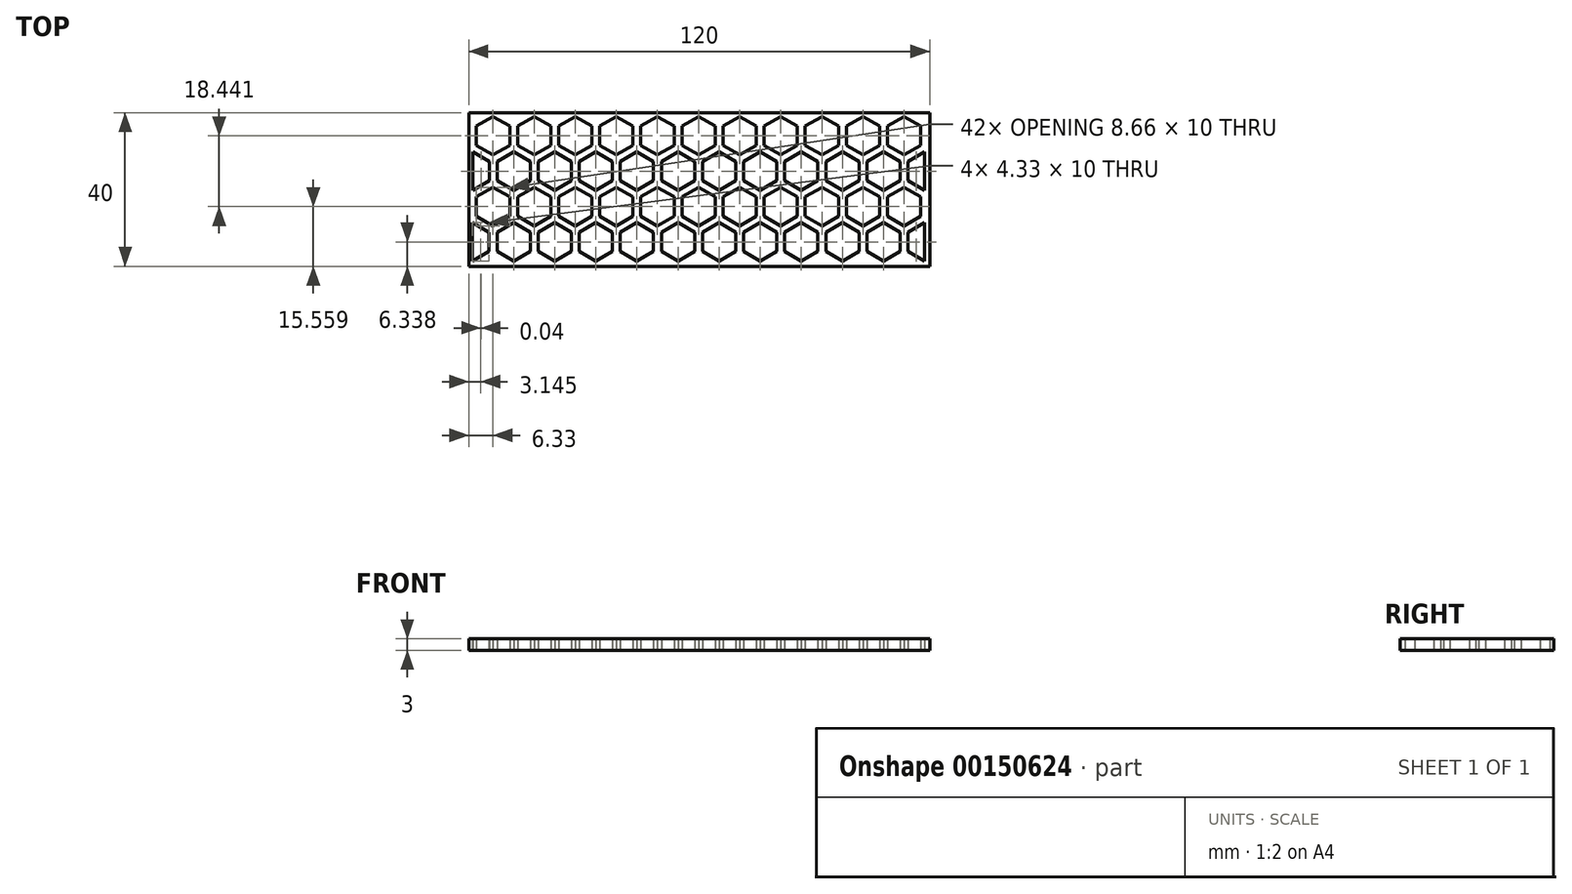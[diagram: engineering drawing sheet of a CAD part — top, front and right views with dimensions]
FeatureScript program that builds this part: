
annotation { "Feature Type Name" : "Feature", "Feature Type Description" : "" }
export const myFeature = defineFeature(function(context is Context, id is Id, definition is map)
    precondition{}
    {
        {
            var Q0;
            Q0=qCreatedBy(makeId("Top.planeOp"),FACE);
            var sketch = newSketch(context, id + "F0", { "sketchPlane" : qUnion([Q0])});
            skCircle(sketch, "E0.cCircle", {"center": v(-53.67, 14) * mm, "radius": 4.33 * mm, "construction": true});
            skLineSegment(sketch, "E0.0", {"start": v(-49.34, 11.5) * mm, "end": v(-53.67, 9) * mm});
            skLineSegment(sketch, "E0.1", {"start": v(-53.67, 9) * mm, "end": v(-58, 11.5) * mm});
            skLineSegment(sketch, "E0.2", {"start": v(-58, 11.5) * mm, "end": v(-58, 16.5) * mm});
            skLineSegment(sketch, "E0.3", {"start": v(-58, 16.5) * mm, "end": v(-53.67, 19) * mm});
            skLineSegment(sketch, "E0.4", {"start": v(-53.67, 19) * mm, "end": v(-49.34, 16.5) * mm});
            skLineSegment(sketch, "E0.5", {"start": v(-49.34, 16.5) * mm, "end": v(-49.34, 11.5) * mm});
            skPoint(sketch, "E0.0.midPoint", {"position": v(-51.5, 10.25) * mm});
            skPoint(sketch, "E1.1.0.0", {"position": v(-40.8, 10.25) * mm});
            skCircle(sketch, "E1.1.0.1", {"center": v(-42.97, 14) * mm, "radius": 4.33 * mm, "construction": true});
            skLineSegment(sketch, "E1.1.0.2", {"start": v(-38.64, 16.5) * mm, "end": v(-38.64, 11.5) * mm});
            skLineSegment(sketch, "E1.1.0.3", {"start": v(-42.97, 19) * mm, "end": v(-38.64, 16.5) * mm});
            skLineSegment(sketch, "E1.1.0.4", {"start": v(-47.3, 16.5) * mm, "end": v(-42.97, 19) * mm});
            skLineSegment(sketch, "E1.1.0.5", {"start": v(-47.3, 11.5) * mm, "end": v(-47.3, 16.5) * mm});
            skLineSegment(sketch, "E1.1.0.6", {"start": v(-38.64, 11.5) * mm, "end": v(-42.97, 9) * mm});
            skLineSegment(sketch, "E1.1.0.7", {"start": v(-42.97, 9) * mm, "end": v(-47.3, 11.5) * mm});
            skPoint(sketch, "E1.2.0.0", {"position": v(-30.1, 10.25) * mm});
            skCircle(sketch, "E1.2.0.1", {"center": v(-32.27, 14) * mm, "radius": 4.33 * mm, "construction": true});
            skLineSegment(sketch, "E1.2.0.2", {"start": v(-27.94, 16.5) * mm, "end": v(-27.94, 11.5) * mm});
            skLineSegment(sketch, "E1.2.0.3", {"start": v(-32.27, 19) * mm, "end": v(-27.94, 16.5) * mm});
            skLineSegment(sketch, "E1.2.0.4", {"start": v(-36.6, 16.5) * mm, "end": v(-32.27, 19) * mm});
            skLineSegment(sketch, "E1.2.0.5", {"start": v(-36.6, 11.5) * mm, "end": v(-36.6, 16.5) * mm});
            skLineSegment(sketch, "E1.2.0.6", {"start": v(-27.94, 11.5) * mm, "end": v(-32.27, 9) * mm});
            skLineSegment(sketch, "E1.2.0.7", {"start": v(-32.27, 9) * mm, "end": v(-36.6, 11.5) * mm});
            skPoint(sketch, "E1.3.0.0", {"position": v(-19.4, 10.25) * mm});
            skCircle(sketch, "E1.3.0.1", {"center": v(-21.57, 14) * mm, "radius": 4.33 * mm, "construction": true});
            skLineSegment(sketch, "E1.3.0.2", {"start": v(-17.24, 16.5) * mm, "end": v(-17.24, 11.5) * mm});
            skLineSegment(sketch, "E1.3.0.3", {"start": v(-21.57, 19) * mm, "end": v(-17.24, 16.5) * mm});
            skLineSegment(sketch, "E1.3.0.4", {"start": v(-25.9, 16.5) * mm, "end": v(-21.57, 19) * mm});
            skLineSegment(sketch, "E1.3.0.5", {"start": v(-25.9, 11.5) * mm, "end": v(-25.9, 16.5) * mm});
            skLineSegment(sketch, "E1.3.0.6", {"start": v(-17.24, 11.5) * mm, "end": v(-21.57, 9) * mm});
            skLineSegment(sketch, "E1.3.0.7", {"start": v(-21.57, 9) * mm, "end": v(-25.9, 11.5) * mm});
            skPoint(sketch, "E1.4.0.0", {"position": v(-8.7, 10.25) * mm});
            skCircle(sketch, "E1.4.0.1", {"center": v(-10.87, 14) * mm, "radius": 4.33 * mm, "construction": true});
            skLineSegment(sketch, "E1.4.0.2", {"start": v(-6.54, 16.5) * mm, "end": v(-6.54, 11.5) * mm});
            skLineSegment(sketch, "E1.4.0.3", {"start": v(-10.87, 19) * mm, "end": v(-6.54, 16.5) * mm});
            skLineSegment(sketch, "E1.4.0.4", {"start": v(-15.2, 16.5) * mm, "end": v(-10.87, 19) * mm});
            skLineSegment(sketch, "E1.4.0.5", {"start": v(-15.2, 11.5) * mm, "end": v(-15.2, 16.5) * mm});
            skLineSegment(sketch, "E1.4.0.6", {"start": v(-6.54, 11.5) * mm, "end": v(-10.87, 9) * mm});
            skLineSegment(sketch, "E1.4.0.7", {"start": v(-10.87, 9) * mm, "end": v(-15.2, 11.5) * mm});
            skPoint(sketch, "E1.5.0.0", {"position": v(2, 10.25) * mm});
            skCircle(sketch, "E1.5.0.1", {"center": v(-0.17, 14) * mm, "radius": 4.33 * mm, "construction": true});
            skLineSegment(sketch, "E1.5.0.2", {"start": v(4.16, 16.5) * mm, "end": v(4.16, 11.5) * mm});
            skLineSegment(sketch, "E1.5.0.3", {"start": v(-0.17, 19) * mm, "end": v(4.16, 16.5) * mm});
            skLineSegment(sketch, "E1.5.0.4", {"start": v(-4.5, 16.5) * mm, "end": v(-0.17, 19) * mm});
            skLineSegment(sketch, "E1.5.0.5", {"start": v(-4.5, 11.5) * mm, "end": v(-4.5, 16.5) * mm});
            skLineSegment(sketch, "E1.5.0.6", {"start": v(4.16, 11.5) * mm, "end": v(-0.17, 9) * mm});
            skLineSegment(sketch, "E1.5.0.7", {"start": v(-0.17, 9) * mm, "end": v(-4.5, 11.5) * mm});
            skPoint(sketch, "E1.6.0.0", {"position": v(12.7, 10.25) * mm});
            skCircle(sketch, "E1.6.0.1", {"center": v(10.53, 14) * mm, "radius": 4.33 * mm, "construction": true});
            skLineSegment(sketch, "E1.6.0.2", {"start": v(14.86, 16.5) * mm, "end": v(14.86, 11.5) * mm});
            skLineSegment(sketch, "E1.6.0.3", {"start": v(10.53, 19) * mm, "end": v(14.86, 16.5) * mm});
            skLineSegment(sketch, "E1.6.0.4", {"start": v(6.2, 16.5) * mm, "end": v(10.53, 19) * mm});
            skLineSegment(sketch, "E1.6.0.5", {"start": v(6.2, 11.5) * mm, "end": v(6.2, 16.5) * mm});
            skLineSegment(sketch, "E1.6.0.6", {"start": v(14.86, 11.5) * mm, "end": v(10.53, 9) * mm});
            skLineSegment(sketch, "E1.6.0.7", {"start": v(10.53, 9) * mm, "end": v(6.2, 11.5) * mm});
            skPoint(sketch, "E1.7.0.0", {"position": v(23.4, 10.25) * mm});
            skCircle(sketch, "E1.7.0.1", {"center": v(21.23, 14) * mm, "radius": 4.33 * mm, "construction": true});
            skLineSegment(sketch, "E1.7.0.2", {"start": v(25.56, 16.5) * mm, "end": v(25.56, 11.5) * mm});
            skLineSegment(sketch, "E1.7.0.3", {"start": v(21.23, 19) * mm, "end": v(25.56, 16.5) * mm});
            skLineSegment(sketch, "E1.7.0.4", {"start": v(16.9, 16.5) * mm, "end": v(21.23, 19) * mm});
            skLineSegment(sketch, "E1.7.0.5", {"start": v(16.9, 11.5) * mm, "end": v(16.9, 16.5) * mm});
            skLineSegment(sketch, "E1.7.0.6", {"start": v(25.56, 11.5) * mm, "end": v(21.23, 9) * mm});
            skLineSegment(sketch, "E1.7.0.7", {"start": v(21.23, 9) * mm, "end": v(16.9, 11.5) * mm});
            skPoint(sketch, "E1.8.0.0", {"position": v(34.1, 10.25) * mm});
            skCircle(sketch, "E1.8.0.1", {"center": v(31.93, 14) * mm, "radius": 4.33 * mm, "construction": true});
            skLineSegment(sketch, "E1.8.0.2", {"start": v(36.26, 16.5) * mm, "end": v(36.26, 11.5) * mm});
            skLineSegment(sketch, "E1.8.0.3", {"start": v(31.93, 19) * mm, "end": v(36.26, 16.5) * mm});
            skLineSegment(sketch, "E1.8.0.4", {"start": v(27.6, 16.5) * mm, "end": v(31.93, 19) * mm});
            skLineSegment(sketch, "E1.8.0.5", {"start": v(27.6, 11.5) * mm, "end": v(27.6, 16.5) * mm});
            skLineSegment(sketch, "E1.8.0.6", {"start": v(36.26, 11.5) * mm, "end": v(31.93, 9) * mm});
            skLineSegment(sketch, "E1.8.0.7", {"start": v(31.93, 9) * mm, "end": v(27.6, 11.5) * mm});
            skPoint(sketch, "E1.9.0.0", {"position": v(44.8, 10.25) * mm});
            skCircle(sketch, "E1.9.0.1", {"center": v(42.63, 14) * mm, "radius": 4.33 * mm, "construction": true});
            skLineSegment(sketch, "E1.9.0.2", {"start": v(46.96, 16.5) * mm, "end": v(46.96, 11.5) * mm});
            skLineSegment(sketch, "E1.9.0.3", {"start": v(42.63, 19) * mm, "end": v(46.96, 16.5) * mm});
            skLineSegment(sketch, "E1.9.0.4", {"start": v(38.3, 16.5) * mm, "end": v(42.63, 19) * mm});
            skLineSegment(sketch, "E1.9.0.5", {"start": v(38.3, 11.5) * mm, "end": v(38.3, 16.5) * mm});
            skLineSegment(sketch, "E1.9.0.6", {"start": v(46.96, 11.5) * mm, "end": v(42.63, 9) * mm});
            skLineSegment(sketch, "E1.9.0.7", {"start": v(42.63, 9) * mm, "end": v(38.3, 11.5) * mm});
            skLineSegment(sketch, "E1.direction1", {"start": v(-58, 11.5) * mm, "end": v(-47.3, 11.5) * mm, "construction": true});
            skCircle(sketch, "E2.cCircle", {"center": v(-53.67, -4.44) * mm, "radius": 4.33 * mm, "construction": true});
            skLineSegment(sketch, "E2.0", {"start": v(-49.34, -6.94) * mm, "end": v(-53.67, -9.44) * mm});
            skLineSegment(sketch, "E2.1", {"start": v(-53.67, -9.44) * mm, "end": v(-58, -6.94) * mm});
            skLineSegment(sketch, "E2.2", {"start": v(-58, -6.94) * mm, "end": v(-58, -1.94) * mm});
            skLineSegment(sketch, "E2.3", {"start": v(-58, -1.94) * mm, "end": v(-53.67, 0.56) * mm});
            skLineSegment(sketch, "E2.4", {"start": v(-53.67, 0.56) * mm, "end": v(-49.34, -1.94) * mm});
            skLineSegment(sketch, "E2.5", {"start": v(-49.34, -1.94) * mm, "end": v(-49.34, -6.94) * mm});
            skPoint(sketch, "E2.0.midPoint", {"position": v(-51.5, -8.2) * mm});
            skPoint(sketch, "E3.1.0.0", {"position": v(-40.8, -8.2) * mm});
            skCircle(sketch, "E3.1.0.1", {"center": v(-42.97, -4.44) * mm, "radius": 4.33 * mm, "construction": true});
            skLineSegment(sketch, "E3.1.0.2", {"start": v(-38.64, -1.94) * mm, "end": v(-38.64, -6.94) * mm});
            skLineSegment(sketch, "E3.1.0.3", {"start": v(-42.97, 0.56) * mm, "end": v(-38.64, -1.94) * mm});
            skLineSegment(sketch, "E3.1.0.4", {"start": v(-47.3, -1.94) * mm, "end": v(-42.97, 0.56) * mm});
            skLineSegment(sketch, "E3.1.0.5", {"start": v(-47.3, -6.94) * mm, "end": v(-47.3, -1.94) * mm});
            skLineSegment(sketch, "E3.1.0.6", {"start": v(-38.64, -6.94) * mm, "end": v(-42.97, -9.44) * mm});
            skLineSegment(sketch, "E3.1.0.7", {"start": v(-42.97, -9.44) * mm, "end": v(-47.3, -6.94) * mm});
            skPoint(sketch, "E3.2.0.0", {"position": v(-30.1, -8.2) * mm});
            skCircle(sketch, "E3.2.0.1", {"center": v(-32.27, -4.44) * mm, "radius": 4.33 * mm, "construction": true});
            skLineSegment(sketch, "E3.2.0.2", {"start": v(-27.94, -1.94) * mm, "end": v(-27.94, -6.94) * mm});
            skLineSegment(sketch, "E3.2.0.3", {"start": v(-32.27, 0.56) * mm, "end": v(-27.94, -1.94) * mm});
            skLineSegment(sketch, "E3.2.0.4", {"start": v(-36.6, -1.94) * mm, "end": v(-32.27, 0.56) * mm});
            skLineSegment(sketch, "E3.2.0.5", {"start": v(-36.6, -6.94) * mm, "end": v(-36.6, -1.94) * mm});
            skLineSegment(sketch, "E3.2.0.6", {"start": v(-27.94, -6.94) * mm, "end": v(-32.27, -9.44) * mm});
            skLineSegment(sketch, "E3.2.0.7", {"start": v(-32.27, -9.44) * mm, "end": v(-36.6, -6.94) * mm});
            skPoint(sketch, "E3.3.0.0", {"position": v(-19.4, -8.2) * mm});
            skCircle(sketch, "E3.3.0.1", {"center": v(-21.57, -4.44) * mm, "radius": 4.33 * mm, "construction": true});
            skLineSegment(sketch, "E3.3.0.2", {"start": v(-17.24, -1.94) * mm, "end": v(-17.24, -6.94) * mm});
            skLineSegment(sketch, "E3.3.0.3", {"start": v(-21.57, 0.56) * mm, "end": v(-17.24, -1.94) * mm});
            skLineSegment(sketch, "E3.3.0.4", {"start": v(-25.9, -1.94) * mm, "end": v(-21.57, 0.56) * mm});
            skLineSegment(sketch, "E3.3.0.5", {"start": v(-25.9, -6.94) * mm, "end": v(-25.9, -1.94) * mm});
            skLineSegment(sketch, "E3.3.0.6", {"start": v(-17.24, -6.94) * mm, "end": v(-21.57, -9.44) * mm});
            skLineSegment(sketch, "E3.3.0.7", {"start": v(-21.57, -9.44) * mm, "end": v(-25.9, -6.94) * mm});
            skPoint(sketch, "E3.4.0.0", {"position": v(-8.7, -8.2) * mm});
            skCircle(sketch, "E3.4.0.1", {"center": v(-10.87, -4.44) * mm, "radius": 4.33 * mm, "construction": true});
            skLineSegment(sketch, "E3.4.0.2", {"start": v(-6.54, -1.94) * mm, "end": v(-6.54, -6.94) * mm});
            skLineSegment(sketch, "E3.4.0.3", {"start": v(-10.87, 0.56) * mm, "end": v(-6.54, -1.94) * mm});
            skLineSegment(sketch, "E3.4.0.4", {"start": v(-15.2, -1.94) * mm, "end": v(-10.87, 0.56) * mm});
            skLineSegment(sketch, "E3.4.0.5", {"start": v(-15.2, -6.94) * mm, "end": v(-15.2, -1.94) * mm});
            skLineSegment(sketch, "E3.4.0.6", {"start": v(-6.54, -6.94) * mm, "end": v(-10.87, -9.44) * mm});
            skLineSegment(sketch, "E3.4.0.7", {"start": v(-10.87, -9.44) * mm, "end": v(-15.2, -6.94) * mm});
            skPoint(sketch, "E3.5.0.0", {"position": v(2, -8.2) * mm});
            skCircle(sketch, "E3.5.0.1", {"center": v(-0.17, -4.44) * mm, "radius": 4.33 * mm, "construction": true});
            skLineSegment(sketch, "E3.5.0.2", {"start": v(4.16, -1.94) * mm, "end": v(4.16, -6.94) * mm});
            skLineSegment(sketch, "E3.5.0.3", {"start": v(-0.17, 0.56) * mm, "end": v(4.16, -1.94) * mm});
            skLineSegment(sketch, "E3.5.0.4", {"start": v(-4.5, -1.94) * mm, "end": v(-0.17, 0.56) * mm});
            skLineSegment(sketch, "E3.5.0.5", {"start": v(-4.5, -6.94) * mm, "end": v(-4.5, -1.94) * mm});
            skLineSegment(sketch, "E3.5.0.6", {"start": v(4.16, -6.94) * mm, "end": v(-0.17, -9.44) * mm});
            skLineSegment(sketch, "E3.5.0.7", {"start": v(-0.17, -9.44) * mm, "end": v(-4.5, -6.94) * mm});
            skPoint(sketch, "E3.6.0.0", {"position": v(12.7, -8.2) * mm});
            skCircle(sketch, "E3.6.0.1", {"center": v(10.53, -4.44) * mm, "radius": 4.33 * mm, "construction": true});
            skLineSegment(sketch, "E3.6.0.2", {"start": v(14.86, -1.94) * mm, "end": v(14.86, -6.94) * mm});
            skLineSegment(sketch, "E3.6.0.3", {"start": v(10.53, 0.56) * mm, "end": v(14.86, -1.94) * mm});
            skLineSegment(sketch, "E3.6.0.4", {"start": v(6.2, -1.94) * mm, "end": v(10.53, 0.56) * mm});
            skLineSegment(sketch, "E3.6.0.5", {"start": v(6.2, -6.94) * mm, "end": v(6.2, -1.94) * mm});
            skLineSegment(sketch, "E3.6.0.6", {"start": v(14.86, -6.94) * mm, "end": v(10.53, -9.44) * mm});
            skLineSegment(sketch, "E3.6.0.7", {"start": v(10.53, -9.44) * mm, "end": v(6.2, -6.94) * mm});
            skPoint(sketch, "E3.7.0.0", {"position": v(23.4, -8.2) * mm});
            skCircle(sketch, "E3.7.0.1", {"center": v(21.23, -4.44) * mm, "radius": 4.33 * mm, "construction": true});
            skLineSegment(sketch, "E3.7.0.2", {"start": v(25.56, -1.94) * mm, "end": v(25.56, -6.94) * mm});
            skLineSegment(sketch, "E3.7.0.3", {"start": v(21.23, 0.56) * mm, "end": v(25.56, -1.94) * mm});
            skLineSegment(sketch, "E3.7.0.4", {"start": v(16.9, -1.94) * mm, "end": v(21.23, 0.56) * mm});
            skLineSegment(sketch, "E3.7.0.5", {"start": v(16.9, -6.94) * mm, "end": v(16.9, -1.94) * mm});
            skLineSegment(sketch, "E3.7.0.6", {"start": v(25.56, -6.94) * mm, "end": v(21.23, -9.44) * mm});
            skLineSegment(sketch, "E3.7.0.7", {"start": v(21.23, -9.44) * mm, "end": v(16.9, -6.94) * mm});
            skPoint(sketch, "E3.8.0.0", {"position": v(34.1, -8.2) * mm});
            skCircle(sketch, "E3.8.0.1", {"center": v(31.93, -4.44) * mm, "radius": 4.33 * mm, "construction": true});
            skLineSegment(sketch, "E3.8.0.2", {"start": v(36.26, -1.94) * mm, "end": v(36.26, -6.94) * mm});
            skLineSegment(sketch, "E3.8.0.3", {"start": v(31.93, 0.56) * mm, "end": v(36.26, -1.94) * mm});
            skLineSegment(sketch, "E3.8.0.4", {"start": v(27.6, -1.94) * mm, "end": v(31.93, 0.56) * mm});
            skLineSegment(sketch, "E3.8.0.5", {"start": v(27.6, -6.94) * mm, "end": v(27.6, -1.94) * mm});
            skLineSegment(sketch, "E3.8.0.6", {"start": v(36.26, -6.94) * mm, "end": v(31.93, -9.44) * mm});
            skLineSegment(sketch, "E3.8.0.7", {"start": v(31.93, -9.44) * mm, "end": v(27.6, -6.94) * mm});
            skPoint(sketch, "E3.9.0.0", {"position": v(44.8, -8.2) * mm});
            skCircle(sketch, "E3.9.0.1", {"center": v(42.63, -4.44) * mm, "radius": 4.33 * mm, "construction": true});
            skLineSegment(sketch, "E3.9.0.2", {"start": v(46.96, -1.94) * mm, "end": v(46.96, -6.94) * mm});
            skLineSegment(sketch, "E3.9.0.3", {"start": v(42.63, 0.56) * mm, "end": v(46.96, -1.94) * mm});
            skLineSegment(sketch, "E3.9.0.4", {"start": v(38.3, -1.94) * mm, "end": v(42.63, 0.56) * mm});
            skLineSegment(sketch, "E3.9.0.5", {"start": v(38.3, -6.94) * mm, "end": v(38.3, -1.94) * mm});
            skLineSegment(sketch, "E3.9.0.6", {"start": v(46.96, -6.94) * mm, "end": v(42.63, -9.44) * mm});
            skLineSegment(sketch, "E3.9.0.7", {"start": v(42.63, -9.44) * mm, "end": v(38.3, -6.94) * mm});
            skLineSegment(sketch, "E3.direction1", {"start": v(-58, -6.94) * mm, "end": v(-47.3, -6.94) * mm, "construction": true});
            skCircle(sketch, "E4.cCircle", {"center": v(-48.32, 4.78) * mm, "radius": 4.33 * mm, "construction": true});
            skLineSegment(sketch, "E4.0", {"start": v(-43.99, 2.28) * mm, "end": v(-48.32, -0.22) * mm});
            skLineSegment(sketch, "E4.1", {"start": v(-48.32, -0.22) * mm, "end": v(-52.65, 2.28) * mm});
            skLineSegment(sketch, "E4.2", {"start": v(-52.65, 2.28) * mm, "end": v(-52.65, 7.28) * mm});
            skLineSegment(sketch, "E4.3", {"start": v(-52.65, 7.28) * mm, "end": v(-48.32, 9.78) * mm});
            skLineSegment(sketch, "E4.4", {"start": v(-48.32, 9.78) * mm, "end": v(-43.99, 7.28) * mm});
            skLineSegment(sketch, "E4.5", {"start": v(-43.99, 7.28) * mm, "end": v(-43.99, 2.28) * mm});
            skPoint(sketch, "E4.0.midPoint", {"position": v(-46.15, 1.03) * mm});
            skPoint(sketch, "E5.1.0.0", {"position": v(-35.45, 1.03) * mm});
            skCircle(sketch, "E5.1.0.1", {"center": v(-37.62, 4.78) * mm, "radius": 4.33 * mm, "construction": true});
            skLineSegment(sketch, "E5.1.0.2", {"start": v(-33.29, 7.28) * mm, "end": v(-33.29, 2.28) * mm});
            skLineSegment(sketch, "E5.1.0.3", {"start": v(-37.62, 9.78) * mm, "end": v(-33.29, 7.28) * mm});
            skLineSegment(sketch, "E5.1.0.4", {"start": v(-41.95, 7.28) * mm, "end": v(-37.62, 9.78) * mm});
            skLineSegment(sketch, "E5.1.0.5", {"start": v(-41.95, 2.28) * mm, "end": v(-41.95, 7.28) * mm});
            skLineSegment(sketch, "E5.1.0.6", {"start": v(-33.29, 2.28) * mm, "end": v(-37.62, -0.22) * mm});
            skLineSegment(sketch, "E5.1.0.7", {"start": v(-37.62, -0.22) * mm, "end": v(-41.95, 2.28) * mm});
            skPoint(sketch, "E5.2.0.0", {"position": v(-24.75, 1.03) * mm});
            skCircle(sketch, "E5.2.0.1", {"center": v(-26.92, 4.78) * mm, "radius": 4.33 * mm, "construction": true});
            skLineSegment(sketch, "E5.2.0.2", {"start": v(-22.59, 7.28) * mm, "end": v(-22.59, 2.28) * mm});
            skLineSegment(sketch, "E5.2.0.3", {"start": v(-26.92, 9.78) * mm, "end": v(-22.59, 7.28) * mm});
            skLineSegment(sketch, "E5.2.0.4", {"start": v(-31.25, 7.28) * mm, "end": v(-26.92, 9.78) * mm});
            skLineSegment(sketch, "E5.2.0.5", {"start": v(-31.25, 2.28) * mm, "end": v(-31.25, 7.28) * mm});
            skLineSegment(sketch, "E5.2.0.6", {"start": v(-22.59, 2.28) * mm, "end": v(-26.92, -0.22) * mm});
            skLineSegment(sketch, "E5.2.0.7", {"start": v(-26.92, -0.22) * mm, "end": v(-31.25, 2.28) * mm});
            skPoint(sketch, "E5.3.0.0", {"position": v(-14.05, 1.03) * mm});
            skCircle(sketch, "E5.3.0.1", {"center": v(-16.22, 4.78) * mm, "radius": 4.33 * mm, "construction": true});
            skLineSegment(sketch, "E5.3.0.2", {"start": v(-11.89, 7.28) * mm, "end": v(-11.89, 2.28) * mm});
            skLineSegment(sketch, "E5.3.0.3", {"start": v(-16.22, 9.78) * mm, "end": v(-11.89, 7.28) * mm});
            skLineSegment(sketch, "E5.3.0.4", {"start": v(-20.55, 7.28) * mm, "end": v(-16.22, 9.78) * mm});
            skLineSegment(sketch, "E5.3.0.5", {"start": v(-20.55, 2.28) * mm, "end": v(-20.55, 7.28) * mm});
            skLineSegment(sketch, "E5.3.0.6", {"start": v(-11.89, 2.28) * mm, "end": v(-16.22, -0.22) * mm});
            skLineSegment(sketch, "E5.3.0.7", {"start": v(-16.22, -0.22) * mm, "end": v(-20.55, 2.28) * mm});
            skPoint(sketch, "E5.4.0.0", {"position": v(-3.35, 1.03) * mm});
            skCircle(sketch, "E5.4.0.1", {"center": v(-5.52, 4.78) * mm, "radius": 4.33 * mm, "construction": true});
            skLineSegment(sketch, "E5.4.0.2", {"start": v(-1.19, 7.28) * mm, "end": v(-1.19, 2.28) * mm});
            skLineSegment(sketch, "E5.4.0.3", {"start": v(-5.52, 9.78) * mm, "end": v(-1.19, 7.28) * mm});
            skLineSegment(sketch, "E5.4.0.4", {"start": v(-9.85, 7.28) * mm, "end": v(-5.52, 9.78) * mm});
            skLineSegment(sketch, "E5.4.0.5", {"start": v(-9.85, 2.28) * mm, "end": v(-9.85, 7.28) * mm});
            skLineSegment(sketch, "E5.4.0.6", {"start": v(-1.19, 2.28) * mm, "end": v(-5.52, -0.22) * mm});
            skLineSegment(sketch, "E5.4.0.7", {"start": v(-5.52, -0.22) * mm, "end": v(-9.85, 2.28) * mm});
            skPoint(sketch, "E5.5.0.0", {"position": v(7.35, 1.03) * mm});
            skCircle(sketch, "E5.5.0.1", {"center": v(5.18, 4.78) * mm, "radius": 4.33 * mm, "construction": true});
            skLineSegment(sketch, "E5.5.0.2", {"start": v(9.51, 7.28) * mm, "end": v(9.51, 2.28) * mm});
            skLineSegment(sketch, "E5.5.0.3", {"start": v(5.18, 9.78) * mm, "end": v(9.51, 7.28) * mm});
            skLineSegment(sketch, "E5.5.0.4", {"start": v(0.85, 7.28) * mm, "end": v(5.18, 9.78) * mm});
            skLineSegment(sketch, "E5.5.0.5", {"start": v(0.85, 2.28) * mm, "end": v(0.85, 7.28) * mm});
            skLineSegment(sketch, "E5.5.0.6", {"start": v(9.51, 2.28) * mm, "end": v(5.18, -0.22) * mm});
            skLineSegment(sketch, "E5.5.0.7", {"start": v(5.18, -0.22) * mm, "end": v(0.85, 2.28) * mm});
            skPoint(sketch, "E5.6.0.0", {"position": v(18.05, 1.03) * mm});
            skCircle(sketch, "E5.6.0.1", {"center": v(15.88, 4.78) * mm, "radius": 4.33 * mm, "construction": true});
            skLineSegment(sketch, "E5.6.0.2", {"start": v(20.21, 7.28) * mm, "end": v(20.21, 2.28) * mm});
            skLineSegment(sketch, "E5.6.0.3", {"start": v(15.88, 9.78) * mm, "end": v(20.21, 7.28) * mm});
            skLineSegment(sketch, "E5.6.0.4", {"start": v(11.55, 7.28) * mm, "end": v(15.88, 9.78) * mm});
            skLineSegment(sketch, "E5.6.0.5", {"start": v(11.55, 2.28) * mm, "end": v(11.55, 7.28) * mm});
            skLineSegment(sketch, "E5.6.0.6", {"start": v(20.21, 2.28) * mm, "end": v(15.88, -0.22) * mm});
            skLineSegment(sketch, "E5.6.0.7", {"start": v(15.88, -0.22) * mm, "end": v(11.55, 2.28) * mm});
            skPoint(sketch, "E5.7.0.0", {"position": v(28.75, 1.03) * mm});
            skCircle(sketch, "E5.7.0.1", {"center": v(26.58, 4.78) * mm, "radius": 4.33 * mm, "construction": true});
            skLineSegment(sketch, "E5.7.0.2", {"start": v(30.91, 7.28) * mm, "end": v(30.91, 2.28) * mm});
            skLineSegment(sketch, "E5.7.0.3", {"start": v(26.58, 9.78) * mm, "end": v(30.91, 7.28) * mm});
            skLineSegment(sketch, "E5.7.0.4", {"start": v(22.25, 7.28) * mm, "end": v(26.58, 9.78) * mm});
            skLineSegment(sketch, "E5.7.0.5", {"start": v(22.25, 2.28) * mm, "end": v(22.25, 7.28) * mm});
            skLineSegment(sketch, "E5.7.0.6", {"start": v(30.91, 2.28) * mm, "end": v(26.58, -0.22) * mm});
            skLineSegment(sketch, "E5.7.0.7", {"start": v(26.58, -0.22) * mm, "end": v(22.25, 2.28) * mm});
            skPoint(sketch, "E5.8.0.0", {"position": v(39.45, 1.03) * mm});
            skCircle(sketch, "E5.8.0.1", {"center": v(37.28, 4.78) * mm, "radius": 4.33 * mm, "construction": true});
            skLineSegment(sketch, "E5.8.0.2", {"start": v(41.61, 7.28) * mm, "end": v(41.61, 2.28) * mm});
            skLineSegment(sketch, "E5.8.0.3", {"start": v(37.28, 9.78) * mm, "end": v(41.61, 7.28) * mm});
            skLineSegment(sketch, "E5.8.0.4", {"start": v(32.95, 7.28) * mm, "end": v(37.28, 9.78) * mm});
            skLineSegment(sketch, "E5.8.0.5", {"start": v(32.95, 2.28) * mm, "end": v(32.95, 7.28) * mm});
            skLineSegment(sketch, "E5.8.0.6", {"start": v(41.61, 2.28) * mm, "end": v(37.28, -0.22) * mm});
            skLineSegment(sketch, "E5.8.0.7", {"start": v(37.28, -0.22) * mm, "end": v(32.95, 2.28) * mm});
            skPoint(sketch, "E5.9.0.0", {"position": v(50.15, 1.03) * mm});
            skCircle(sketch, "E5.9.0.1", {"center": v(47.98, 4.78) * mm, "radius": 4.33 * mm, "construction": true});
            skLineSegment(sketch, "E5.9.0.2", {"start": v(52.31, 7.28) * mm, "end": v(52.31, 2.28) * mm});
            skLineSegment(sketch, "E5.9.0.3", {"start": v(47.98, 9.78) * mm, "end": v(52.31, 7.28) * mm});
            skLineSegment(sketch, "E5.9.0.4", {"start": v(43.65, 7.28) * mm, "end": v(47.98, 9.78) * mm});
            skLineSegment(sketch, "E5.9.0.5", {"start": v(43.65, 2.28) * mm, "end": v(43.65, 7.28) * mm});
            skLineSegment(sketch, "E5.9.0.6", {"start": v(52.31, 2.28) * mm, "end": v(47.98, -0.22) * mm});
            skLineSegment(sketch, "E5.9.0.7", {"start": v(47.98, -0.22) * mm, "end": v(43.65, 2.28) * mm});
            skLineSegment(sketch, "E5.direction1", {"start": v(-52.65, 2.28) * mm, "end": v(-41.95, 2.28) * mm, "construction": true});
            skLineSegment(sketch, "E6.cCircle", {"start": v(-62.56, -16.16) * mm, "end": v(-62.56, -16.16) * mm});
            skLineSegment(sketch, "E6.0", {"start": v(-54.69, -16.16) * mm, "end": v(-59.02, -18.66) * mm});
            skLineSegment(sketch, "E6.4", {"start": v(-59.02, -8.66) * mm, "end": v(-54.69, -11.16) * mm});
            skLineSegment(sketch, "E6.5", {"start": v(-54.69, -11.16) * mm, "end": v(-54.69, -16.16) * mm});
            skPoint(sketch, "E6.0.midPoint", {"position": v(-56.85, -17.41) * mm});
            skPoint(sketch, "E7.1.0.0", {"position": v(-46.15, -17.41) * mm});
            skCircle(sketch, "E7.1.0.1", {"center": v(-48.32, -13.66) * mm, "radius": 4.33 * mm, "construction": true});
            skLineSegment(sketch, "E7.1.0.2", {"start": v(-43.99, -11.16) * mm, "end": v(-43.99, -16.16) * mm});
            skLineSegment(sketch, "E7.1.0.3", {"start": v(-48.32, -8.66) * mm, "end": v(-43.99, -11.16) * mm});
            skLineSegment(sketch, "E7.1.0.4", {"start": v(-52.65, -11.16) * mm, "end": v(-48.32, -8.66) * mm});
            skLineSegment(sketch, "E7.1.0.5", {"start": v(-52.65, -16.16) * mm, "end": v(-52.65, -11.16) * mm});
            skLineSegment(sketch, "E7.1.0.6", {"start": v(-43.99, -16.16) * mm, "end": v(-48.32, -18.66) * mm});
            skLineSegment(sketch, "E7.1.0.7", {"start": v(-48.32, -18.66) * mm, "end": v(-52.65, -16.16) * mm});
            skPoint(sketch, "E7.2.0.0", {"position": v(-35.45, -17.41) * mm});
            skCircle(sketch, "E7.2.0.1", {"center": v(-37.62, -13.66) * mm, "radius": 4.33 * mm, "construction": true});
            skLineSegment(sketch, "E7.2.0.2", {"start": v(-33.29, -11.16) * mm, "end": v(-33.29, -16.16) * mm});
            skLineSegment(sketch, "E7.2.0.3", {"start": v(-37.62, -8.66) * mm, "end": v(-33.29, -11.16) * mm});
            skLineSegment(sketch, "E7.2.0.4", {"start": v(-41.95, -11.16) * mm, "end": v(-37.62, -8.66) * mm});
            skLineSegment(sketch, "E7.2.0.5", {"start": v(-41.95, -16.16) * mm, "end": v(-41.95, -11.16) * mm});
            skLineSegment(sketch, "E7.2.0.6", {"start": v(-33.29, -16.16) * mm, "end": v(-37.62, -18.66) * mm});
            skLineSegment(sketch, "E7.2.0.7", {"start": v(-37.62, -18.66) * mm, "end": v(-41.95, -16.16) * mm});
            skPoint(sketch, "E7.3.0.0", {"position": v(-24.75, -17.41) * mm});
            skCircle(sketch, "E7.3.0.1", {"center": v(-26.92, -13.66) * mm, "radius": 4.33 * mm, "construction": true});
            skLineSegment(sketch, "E7.3.0.2", {"start": v(-22.59, -11.16) * mm, "end": v(-22.59, -16.16) * mm});
            skLineSegment(sketch, "E7.3.0.3", {"start": v(-26.92, -8.66) * mm, "end": v(-22.59, -11.16) * mm});
            skLineSegment(sketch, "E7.3.0.4", {"start": v(-31.25, -11.16) * mm, "end": v(-26.92, -8.66) * mm});
            skLineSegment(sketch, "E7.3.0.5", {"start": v(-31.25, -16.16) * mm, "end": v(-31.25, -11.16) * mm});
            skLineSegment(sketch, "E7.3.0.6", {"start": v(-22.59, -16.16) * mm, "end": v(-26.92, -18.66) * mm});
            skLineSegment(sketch, "E7.3.0.7", {"start": v(-26.92, -18.66) * mm, "end": v(-31.25, -16.16) * mm});
            skPoint(sketch, "E7.4.0.0", {"position": v(-14.05, -17.41) * mm});
            skCircle(sketch, "E7.4.0.1", {"center": v(-16.22, -13.66) * mm, "radius": 4.33 * mm, "construction": true});
            skLineSegment(sketch, "E7.4.0.2", {"start": v(-11.89, -11.16) * mm, "end": v(-11.89, -16.16) * mm});
            skLineSegment(sketch, "E7.4.0.3", {"start": v(-16.22, -8.66) * mm, "end": v(-11.89, -11.16) * mm});
            skLineSegment(sketch, "E7.4.0.4", {"start": v(-20.55, -11.16) * mm, "end": v(-16.22, -8.66) * mm});
            skLineSegment(sketch, "E7.4.0.5", {"start": v(-20.55, -16.16) * mm, "end": v(-20.55, -11.16) * mm});
            skLineSegment(sketch, "E7.4.0.6", {"start": v(-11.89, -16.16) * mm, "end": v(-16.22, -18.66) * mm});
            skLineSegment(sketch, "E7.4.0.7", {"start": v(-16.22, -18.66) * mm, "end": v(-20.55, -16.16) * mm});
            skPoint(sketch, "E7.5.0.0", {"position": v(-3.35, -17.41) * mm});
            skCircle(sketch, "E7.5.0.1", {"center": v(-5.52, -13.66) * mm, "radius": 4.33 * mm, "construction": true});
            skLineSegment(sketch, "E7.5.0.2", {"start": v(-1.19, -11.16) * mm, "end": v(-1.19, -16.16) * mm});
            skLineSegment(sketch, "E7.5.0.3", {"start": v(-5.52, -8.66) * mm, "end": v(-1.19, -11.16) * mm});
            skLineSegment(sketch, "E7.5.0.4", {"start": v(-9.85, -11.16) * mm, "end": v(-5.52, -8.66) * mm});
            skLineSegment(sketch, "E7.5.0.5", {"start": v(-9.85, -16.16) * mm, "end": v(-9.85, -11.16) * mm});
            skLineSegment(sketch, "E7.5.0.6", {"start": v(-1.19, -16.16) * mm, "end": v(-5.52, -18.66) * mm});
            skLineSegment(sketch, "E7.5.0.7", {"start": v(-5.52, -18.66) * mm, "end": v(-9.85, -16.16) * mm});
            skPoint(sketch, "E7.6.0.0", {"position": v(7.35, -17.41) * mm});
            skCircle(sketch, "E7.6.0.1", {"center": v(5.18, -13.66) * mm, "radius": 4.33 * mm, "construction": true});
            skLineSegment(sketch, "E7.6.0.2", {"start": v(9.51, -11.16) * mm, "end": v(9.51, -16.16) * mm});
            skLineSegment(sketch, "E7.6.0.3", {"start": v(5.18, -8.66) * mm, "end": v(9.51, -11.16) * mm});
            skLineSegment(sketch, "E7.6.0.4", {"start": v(0.85, -11.16) * mm, "end": v(5.18, -8.66) * mm});
            skLineSegment(sketch, "E7.6.0.5", {"start": v(0.85, -16.16) * mm, "end": v(0.85, -11.16) * mm});
            skLineSegment(sketch, "E7.6.0.6", {"start": v(9.51, -16.16) * mm, "end": v(5.18, -18.66) * mm});
            skLineSegment(sketch, "E7.6.0.7", {"start": v(5.18, -18.66) * mm, "end": v(0.85, -16.16) * mm});
            skPoint(sketch, "E7.7.0.0", {"position": v(18.05, -17.41) * mm});
            skCircle(sketch, "E7.7.0.1", {"center": v(15.88, -13.66) * mm, "radius": 4.33 * mm, "construction": true});
            skLineSegment(sketch, "E7.7.0.2", {"start": v(20.21, -11.16) * mm, "end": v(20.21, -16.16) * mm});
            skLineSegment(sketch, "E7.7.0.3", {"start": v(15.88, -8.66) * mm, "end": v(20.21, -11.16) * mm});
            skLineSegment(sketch, "E7.7.0.4", {"start": v(11.55, -11.16) * mm, "end": v(15.88, -8.66) * mm});
            skLineSegment(sketch, "E7.7.0.5", {"start": v(11.55, -16.16) * mm, "end": v(11.55, -11.16) * mm});
            skLineSegment(sketch, "E7.7.0.6", {"start": v(20.21, -16.16) * mm, "end": v(15.88, -18.66) * mm});
            skLineSegment(sketch, "E7.7.0.7", {"start": v(15.88, -18.66) * mm, "end": v(11.55, -16.16) * mm});
            skPoint(sketch, "E7.8.0.0", {"position": v(28.75, -17.41) * mm});
            skCircle(sketch, "E7.8.0.1", {"center": v(26.58, -13.66) * mm, "radius": 4.33 * mm, "construction": true});
            skLineSegment(sketch, "E7.8.0.2", {"start": v(30.91, -11.16) * mm, "end": v(30.91, -16.16) * mm});
            skLineSegment(sketch, "E7.8.0.3", {"start": v(26.58, -8.66) * mm, "end": v(30.91, -11.16) * mm});
            skLineSegment(sketch, "E7.8.0.4", {"start": v(22.25, -11.16) * mm, "end": v(26.58, -8.66) * mm});
            skLineSegment(sketch, "E7.8.0.5", {"start": v(22.25, -16.16) * mm, "end": v(22.25, -11.16) * mm});
            skLineSegment(sketch, "E7.8.0.6", {"start": v(30.91, -16.16) * mm, "end": v(26.58, -18.66) * mm});
            skLineSegment(sketch, "E7.8.0.7", {"start": v(26.58, -18.66) * mm, "end": v(22.25, -16.16) * mm});
            skPoint(sketch, "E7.9.0.0", {"position": v(39.45, -17.41) * mm});
            skCircle(sketch, "E7.9.0.1", {"center": v(37.28, -13.66) * mm, "radius": 4.33 * mm, "construction": true});
            skLineSegment(sketch, "E7.9.0.2", {"start": v(41.61, -11.16) * mm, "end": v(41.61, -16.16) * mm});
            skLineSegment(sketch, "E7.9.0.3", {"start": v(37.28, -8.66) * mm, "end": v(41.61, -11.16) * mm});
            skLineSegment(sketch, "E7.9.0.4", {"start": v(32.95, -11.16) * mm, "end": v(37.28, -8.66) * mm});
            skLineSegment(sketch, "E7.9.0.5", {"start": v(32.95, -16.16) * mm, "end": v(32.95, -11.16) * mm});
            skLineSegment(sketch, "E7.9.0.6", {"start": v(41.61, -16.16) * mm, "end": v(37.28, -18.66) * mm});
            skLineSegment(sketch, "E7.9.0.7", {"start": v(37.28, -18.66) * mm, "end": v(32.95, -16.16) * mm});
            skLineSegment(sketch, "E7.direction1", {"start": v(-63.35, -16.16) * mm, "end": v(-62.56, -16.16) * mm, "construction": true});
            skLineSegment(sketch, "E8.bottom", {"start": v(60, -20) * mm, "end": v(-60, -20) * mm});
            skLineSegment(sketch, "E8.top", {"start": v(60, 20) * mm, "end": v(-60, 20) * mm});
            skLineSegment(sketch, "E8.left", {"start": v(60, -20) * mm, "end": v(60, 20) * mm});
            skLineSegment(sketch, "E8.right", {"start": v(-60, -20) * mm, "end": v(-60, 20) * mm});
            skPoint(sketch, "E8.middle", {"position": v(0, 0) * mm});
            skPoint(sketch, "E9.0.10.0", {"position": v(55.5, 10.25) * mm});
            skCircle(sketch, "E9.1.10.0", {"center": v(53.33, 14) * mm, "radius": 4.33 * mm, "construction": true});
            skLineSegment(sketch, "E9.3.10.0", {"start": v(57.66, 16.5) * mm, "end": v(57.66, 11.5) * mm});
            skLineSegment(sketch, "E9.6.10.0", {"start": v(53.33, 19) * mm, "end": v(57.66, 16.5) * mm});
            skLineSegment(sketch, "E9.9.10.0", {"start": v(49, 16.5) * mm, "end": v(53.33, 19) * mm});
            skLineSegment(sketch, "E9.12.10.0", {"start": v(49, 11.5) * mm, "end": v(49, 16.5) * mm});
            skLineSegment(sketch, "E9.15.10.0", {"start": v(57.66, 11.5) * mm, "end": v(53.33, 9) * mm});
            skLineSegment(sketch, "E9.18.10.0", {"start": v(53.33, 9) * mm, "end": v(49, 11.5) * mm});
            skArc(sketch, "E10.1.10.0", {"start": v(58.68, 9.1) * mm, "mid": v(54.35, 4.78) * mm, "end": v(58.68, 0.45) * mm, "construction": true});
            skLineSegment(sketch, "E10.9.10.0", {"start": v(54.35, 7.28) * mm, "end": v(58.68, 9.78) * mm});
            skLineSegment(sketch, "E10.12.10.0", {"start": v(54.35, 2.28) * mm, "end": v(54.35, 7.28) * mm});
            skLineSegment(sketch, "E10.18.10.0", {"start": v(58.68, -0.22) * mm, "end": v(54.35, 2.28) * mm});
            skPoint(sketch, "E11.0.10.0", {"position": v(55.5, -8.2) * mm});
            skCircle(sketch, "E11.1.10.0", {"center": v(53.33, -4.44) * mm, "radius": 4.33 * mm, "construction": true});
            skLineSegment(sketch, "E11.3.10.0", {"start": v(57.66, -1.94) * mm, "end": v(57.66, -6.94) * mm});
            skLineSegment(sketch, "E11.6.10.0", {"start": v(53.33, 0.56) * mm, "end": v(57.66, -1.94) * mm});
            skLineSegment(sketch, "E11.9.10.0", {"start": v(49, -1.94) * mm, "end": v(53.33, 0.56) * mm});
            skLineSegment(sketch, "E11.12.10.0", {"start": v(49, -6.94) * mm, "end": v(49, -1.94) * mm});
            skLineSegment(sketch, "E11.15.10.0", {"start": v(57.66, -6.94) * mm, "end": v(53.33, -9.44) * mm});
            skLineSegment(sketch, "E11.18.10.0", {"start": v(53.33, -9.44) * mm, "end": v(49, -6.94) * mm});
            skPoint(sketch, "E12.0.10.0", {"position": v(50.15, -17.41) * mm});
            skCircle(sketch, "E12.1.10.0", {"center": v(47.98, -13.66) * mm, "radius": 4.33 * mm, "construction": true});
            skLineSegment(sketch, "E12.3.10.0", {"start": v(52.31, -11.16) * mm, "end": v(52.31, -16.16) * mm});
            skLineSegment(sketch, "E12.6.10.0", {"start": v(47.98, -8.66) * mm, "end": v(52.31, -11.16) * mm});
            skLineSegment(sketch, "E12.9.10.0", {"start": v(43.65, -11.16) * mm, "end": v(47.98, -8.66) * mm});
            skLineSegment(sketch, "E12.12.10.0", {"start": v(43.65, -16.16) * mm, "end": v(43.65, -11.16) * mm});
            skLineSegment(sketch, "E12.15.10.0", {"start": v(52.31, -16.16) * mm, "end": v(47.98, -18.66) * mm});
            skLineSegment(sketch, "E12.18.10.0", {"start": v(47.98, -18.66) * mm, "end": v(43.65, -16.16) * mm});
            skArc(sketch, "E12.1.11.0", {"start": v(58.68, -9.33) * mm, "mid": v(54.35, -13.66) * mm, "end": v(58.68, -18) * mm, "construction": true});
            skLineSegment(sketch, "E12.9.11.0", {"start": v(54.35, -11.16) * mm, "end": v(58.68, -8.66) * mm});
            skLineSegment(sketch, "E12.12.11.0", {"start": v(54.35, -16.16) * mm, "end": v(54.35, -11.16) * mm});
            skLineSegment(sketch, "E12.18.11.0", {"start": v(58.68, -18.66) * mm, "end": v(54.35, -16.16) * mm});
            skArc(sketch, "E13.cCircle", {"start": v(-58.98, 0.43) * mm, "mid": v(-54.65, 4.76) * mm, "end": v(-58.98, 9.09) * mm, "construction": true});
            skLineSegment(sketch, "E13.0", {"start": v(-54.65, 2.26) * mm, "end": v(-58.98, -0.24) * mm});
            skLineSegment(sketch, "E13.4", {"start": v(-58.98, 9.76) * mm, "end": v(-54.65, 7.26) * mm});
            skLineSegment(sketch, "E13.5", {"start": v(-54.65, 7.26) * mm, "end": v(-54.65, 2.26) * mm});
            skPoint(sketch, "E13.0.midPoint", {"position": v(-56.82, 1) * mm});
            skLineSegment(sketch, "E14", {"start": v(58.68, 9.78) * mm, "end": v(58.68, -0.22) * mm});
            skLineSegment(sketch, "E15", {"start": v(58.68, -8.66) * mm, "end": v(58.68, -18.66) * mm});
            skLineSegment(sketch, "E16", {"start": v(-58.98, 9.76) * mm, "end": v(-58.98, -0.24) * mm});
            skLineSegment(sketch, "E17", {"start": v(-59.02, -18.66) * mm, "end": v(-59.02, -8.66) * mm});
            skArc(sketch, "E18.trimOffspring", {"start": v(-59.02, -18) * mm, "mid": v(-54.69, -13.66) * mm, "end": v(-59.02, -9.33) * mm, "construction": true});
            skLineSegment(sketch, "E19.trimOffspring", {"start": v(-59.02, -16.16) * mm, "end": v(-52.65, -16.16) * mm, "construction": true});
            skSolve(sketch);
        }
        {
            var Q0;
            Q0 = qSketchRegion(id + "F0", true);
            extrude(context, id + "F1", {"entities" : qUnion([Q0]), "depth" : 3 * mm});
        }
    });
